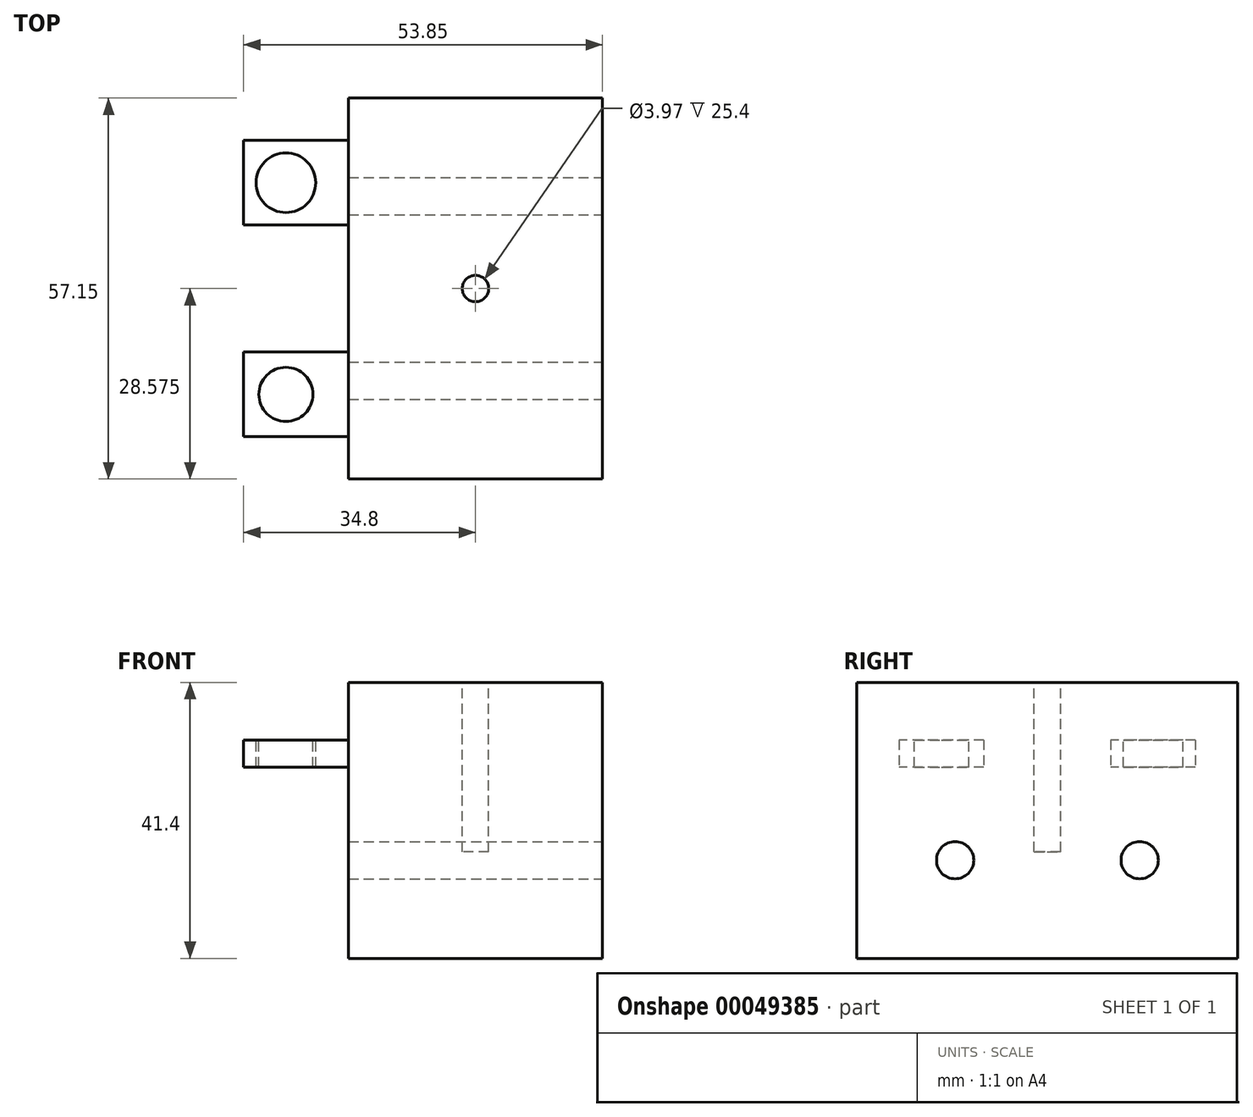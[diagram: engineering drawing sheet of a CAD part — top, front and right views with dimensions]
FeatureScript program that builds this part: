
annotation { "Feature Type Name" : "Feature", "Feature Type Description" : "" }
export const myFeature = defineFeature(function(context is Context, id is Id, definition is map)
    precondition{}
    {
        {
            var Q0;
            Q0=qCreatedBy(makeId("Top.planeOp"),FACE);
            var sketch = newSketch(context, id + "F0", { "sketchPlane" : qUnion([Q0])});
            skLineSegment(sketch, "E0.bottom", {"start": v(0, 0) * mm, "end": v(38.1, 0) * mm});
            skLineSegment(sketch, "E0.top", {"start": v(0, 57.15) * mm, "end": v(38.1, 57.15) * mm});
            skLineSegment(sketch, "E0.left", {"start": v(0, 0) * mm, "end": v(0, 57.15) * mm});
            skLineSegment(sketch, "E0.right", {"start": v(38.1, 0) * mm, "end": v(38.1, 57.15) * mm});
            skSolve(sketch);
        }
        {
            var Q0;
            Q0 = qSketchRegion(id + "F0", true);
            extrude(context, id + "F1", {"entities" : qUnion([Q0]), "depth" : 41.4 * mm});
        }
        {
            var Q0;
            Q0=makeQuery(id+"F1.opExtrude","SWEPT_FACE",FACE,{"disambiguationData":[OSD([sQuery(id+"F0.wireOp",EDGE,"E0.right")])]});
            var sketch = newSketch(context, id + "F2", { "sketchPlane" : qUnion([Q0])});
            skCircle(sketch, "E1", {"center": v(14.73, 14.73) * mm, "radius": 2.8 * mm});
            skCircle(sketch, "E2", {"center": v(42.42, 14.73) * mm, "radius": 2.8 * mm});
            skSolve(sketch);
        }
        {
            var Q0;
            Q0 = qSketchRegion(id + "F2", true);
            extrude(context, id + "F3", {"entities" : qUnion([Q0]), "operationType" : NewBodyOperationType.REMOVE, "endBound" : BoundingType.THROUGH_ALL, "oppositeDirection" : true, "depth" : 25.4 * mm});
        }
        {
            var Q0;
            Q0=makeQuery(id+"F1.opExtrude","CAP_FACE",FACE,{"disambiguationData":[OSD([sQuery(id+"F0.wireOp",EDGE,"E0.bottom"),sQuery(id+"F0.wireOp",EDGE,"E0.top"),sQuery(id+"F0.wireOp",EDGE,"E0.left"),sQuery(id+"F0.wireOp",EDGE,"E0.right")])],"isStart":false});
            var sketch = newSketch(context, id + "F4", { "sketchPlane" : qUnion([Q0])});
            skLineSegment(sketch, "E3", {"start": v(0, 57.15) * mm, "end": v(38.1, 0) * mm, "construction": true});
            skLineSegment(sketch, "E4", {"start": v(38.1, 57.15) * mm, "end": v(0, 0) * mm, "construction": true});
            skPoint(sketch, "E5", {"position": v(19.05, 28.57) * mm});
            skCircle(sketch, "E6", {"center": v(19.05, 28.57) * mm, "radius": 1.98 * mm});
            skSolve(sketch);
        }
        {
            var Q0;
            Q0 = qSketchRegion(id + "F4", true);
            extrude(context, id + "F5", {"entities" : qUnion([Q0]), "operationType" : NewBodyOperationType.REMOVE, "oppositeDirection" : true, "depth" : 25.4 * mm});
        }
        {
            var Q0;
            Q0=makeQuery(id+"F1.opExtrude","SWEPT_FACE",FACE,{"disambiguationData":[OSD([sQuery(id+"F0.wireOp",EDGE,"E0.left")])]});
            var sketch = newSketch(context, id + "F6", { "sketchPlane" : qUnion([Q0])});
            skLineSegment(sketch, "E7.bottom", {"start": v(-50.8, 32.77) * mm, "end": v(-38.1, 32.77) * mm});
            skLineSegment(sketch, "E7.top", {"start": v(-50.8, 28.7) * mm, "end": v(-38.1, 28.7) * mm});
            skLineSegment(sketch, "E7.left", {"start": v(-50.8, 32.77) * mm, "end": v(-50.8, 28.7) * mm});
            skLineSegment(sketch, "E7.right", {"start": v(-38.1, 32.77) * mm, "end": v(-38.1, 28.7) * mm});
            skLineSegment(sketch, "E8.bottom", {"start": v(-19.05, 32.77) * mm, "end": v(-6.35, 32.77) * mm});
            skLineSegment(sketch, "E8.top", {"start": v(-19.05, 28.7) * mm, "end": v(-6.35, 28.7) * mm});
            skLineSegment(sketch, "E8.left", {"start": v(-19.05, 32.77) * mm, "end": v(-19.05, 28.7) * mm});
            skLineSegment(sketch, "E8.right", {"start": v(-6.35, 32.77) * mm, "end": v(-6.35, 28.7) * mm});
            skSolve(sketch);
        }
        {
            var Q0;
            Q0 = qSketchRegion(id + "F6", true);
            extrude(context, id + "F7", {"entities" : qUnion([Q0]), "operationType" : NewBodyOperationType.ADD, "depth" : 15.75 * mm});
        }
        {
            var Q0;
            Q0=makeQuery(id+"F7.opExtrude","SWEPT_FACE",FACE,{"disambiguationData":[OSD([sQuery(id+"F6.wireOp",EDGE,"E7.bottom")])]});
            var sketch = newSketch(context, id + "F8", { "sketchPlane" : qUnion([Q0])});
            skCircle(sketch, "E9", {"center": v(-9.4, 44.45) * mm, "radius": 4.47 * mm});
            skCircle(sketch, "E10", {"center": v(-9.4, 12.7) * mm, "radius": 4.06 * mm});
            skSolve(sketch);
        }
        {
            var Q0;
            Q0 = qSketchRegion(id + "F8", true);
            extrude(context, id + "F9", {"entities" : qUnion([Q0]), "operationType" : NewBodyOperationType.REMOVE, "endBound" : BoundingType.THROUGH_ALL, "oppositeDirection" : true, "depth" : 25.4 * mm});
        }
    });
